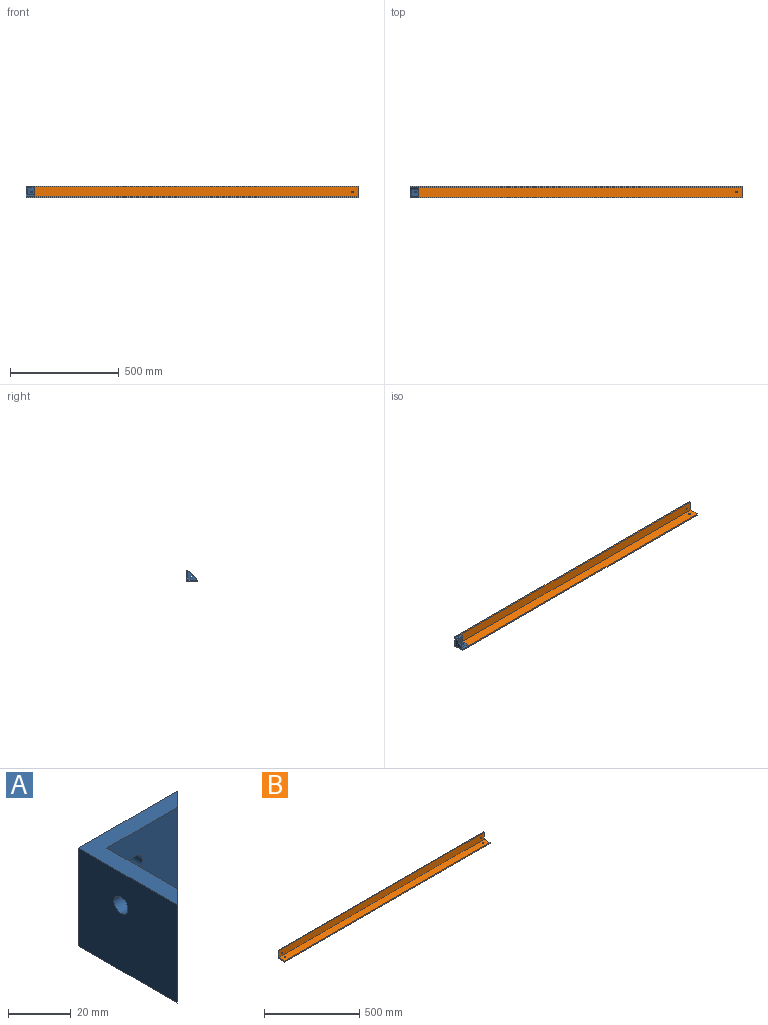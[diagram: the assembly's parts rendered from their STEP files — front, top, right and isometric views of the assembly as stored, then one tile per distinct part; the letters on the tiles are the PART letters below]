
ASSEMBLY  parts=2 mates=1
PART A: 14 faces, bbox 44.5x44.5x38.1 mm
  f0: plane 44.45x38.1mm, normal (-1,0,0), area 1661.9mm2, adj f1,f2,f4,f7,f13
  f1: plane 44.45x44.45mm, normal (0.71,-0.71,0), area 969.4mm2, adj f0,f2,f3,f4,f5,f6,f7
  f2: plane 44.45x38.1mm, normal (0,1,0), area 1661.9mm2, adj f0,f1,f4,f7,f12
  f3: plane 31.75x31.75mm, normal (0,0,1), area 490.5mm2, adj f1,f5,f6,f8,f9,f10,f11
  f4: plane 44.45x44.45mm, normal (0,0,-1), area 974.4mm2, adj f0,f1,f2,f8,f9,f10,f11
  f5: plane 31.75x31.75mm, normal (0,-1,0), area 976.4mm2, adj f1,f3,f6,f7,f12
  f6: plane 31.75x31.75mm, normal (1,0,0), area 976.4mm2, adj f1,f3,f5,f7,f13
  f7: plane 44.45x44.45mm, normal (0,0,1), area 483.9mm2, adj f0,f1,f2,f5,f6
  f8: plane 6.36x6.36mm, normal (0.71,0.71,0), area 57.1mm2, adj f3,f4,f9,f10
  f9: plane 6.35x1.06mm, normal (0.71,-0.71,0), area 9.5mm2, adj f3,f4,f8,f11
  f10: plane 6.35x1.06mm, normal (-0.71,0.71,0), area 9.5mm2, adj f3,f4,f8,f11
  f11: plane 6.36x6.36mm, normal (-0.71,-0.71,0), area 57.1mm2, adj f3,f4,f9,f10
  f12: cylinder r=3.17mm len=6.35mm, axis (0,1,0), area 126.7mm2, adj f2,f5
  f13: cylinder r=3.17mm len=6.35mm, axis (-1,0,0), area 126.7mm2, adj f0,f6
PART B: 12 faces, bbox 1524x50.8x50.8 mm
  f0: plane 1524x44.45mm, normal (0,0,1), area 67678.5mm2, adj f3,f5,f6,f7,f10,f11
  f1: plane 1524x50.8mm, normal (0,0,-1), area 77355.9mm2, adj f2,f5,f6,f7,f10,f11
  f2: plane 1524x50.8mm, normal (0,1,0), area 77355.9mm2, adj f1,f4,f6,f7,f8,f9
  f3: plane 1524x44.45mm, normal (0,-1,0), area 67678.5mm2, adj f0,f4,f6,f7,f8,f9
  f4: plane 1524x6.35mm, normal (0,0,1), area 9677.4mm2, adj f2,f3,f6,f7
  f5: plane 1524x6.35mm, normal (0,-1,0), area 9677.4mm2, adj f0,f1,f6,f7
  f6: plane 50.8x50.8mm, normal (1,0,0), area 604.8mm2, adj f0,f1,f2,f3,f4,f5
  f7: plane 50.8x50.8mm, normal (-1,0,0), area 604.8mm2, adj f0,f1,f2,f3,f4,f5
  f8: cylinder r=3.17mm len=6.35mm, axis (0,1,0), area 126.7mm2, adj f2,f3
  f9: cylinder r=3.17mm len=6.35mm, axis (0,1,0), area 126.7mm2, adj f2,f3
  f10: cylinder r=3.17mm len=6.35mm, axis (0,0,-1), area 126.7mm2, adj f0,f1
  f11: cylinder r=3.17mm len=6.35mm, axis (0,0,-1), area 126.7mm2, adj f0,f1
PLACE A rot(axis=(-0.58,0.58,-0.58),120deg) t=(-762,-25.4,25.4)mm
PLACE B at identity fixed
MATE fastened B.f8 <-> A.f13  axis (0,-1,0) through (-736.6,-6.35,25.4)mm
